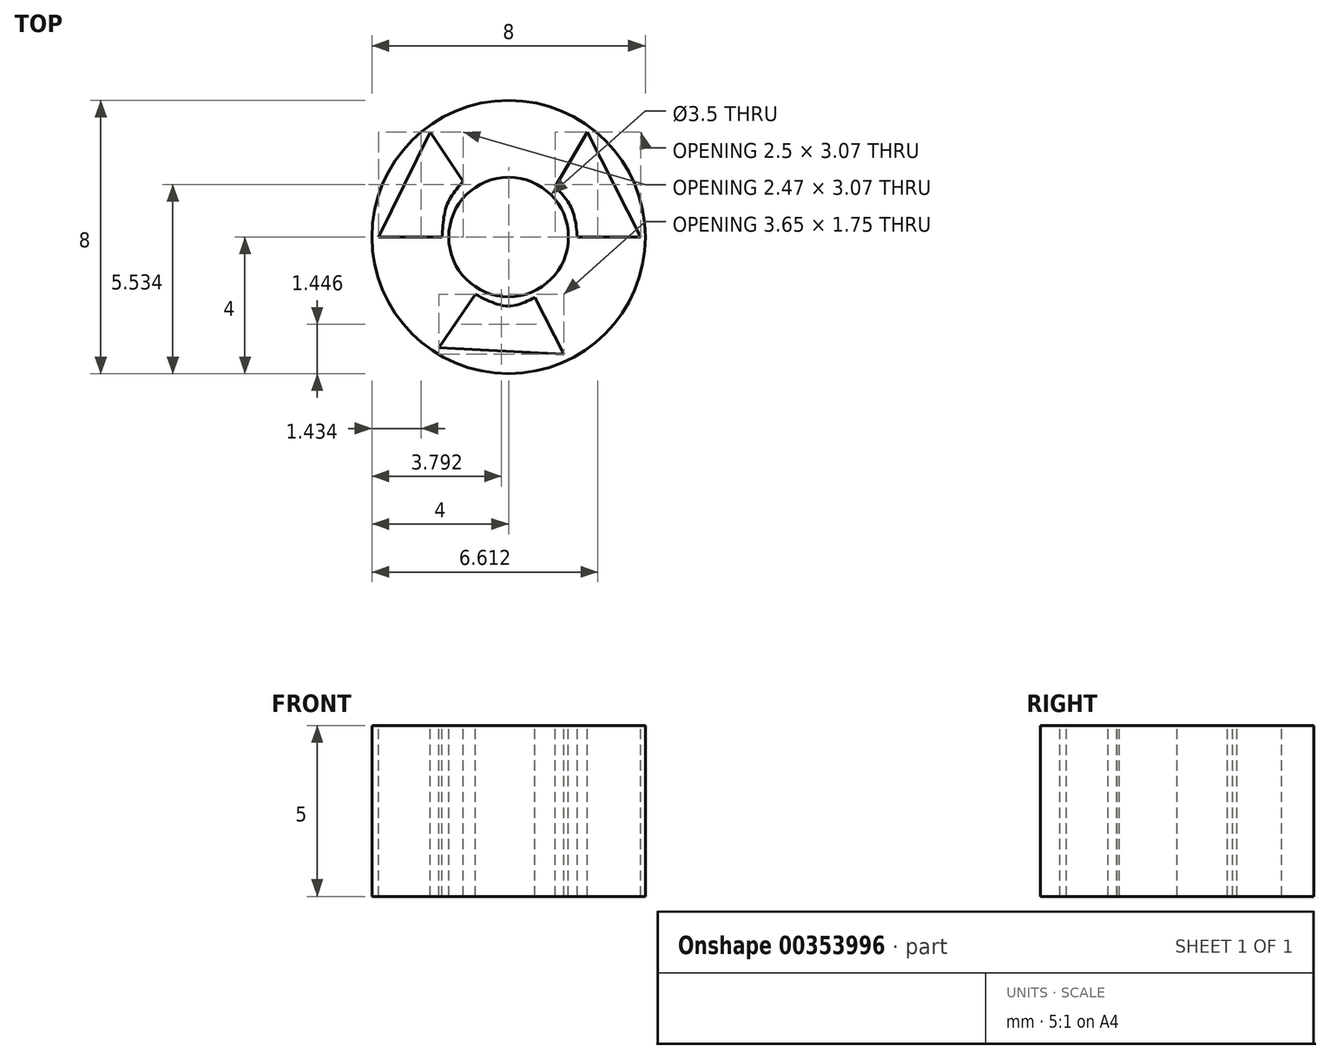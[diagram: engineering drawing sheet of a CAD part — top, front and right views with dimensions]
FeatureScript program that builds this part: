
annotation { "Feature Type Name" : "Feature", "Feature Type Description" : "" }
export const myFeature = defineFeature(function(context is Context, id is Id, definition is map)
    precondition{}
    {
        {
            var Q0;
            Q0=qCreatedBy(makeId("Top.planeOp"),FACE);
            var sketch = newSketch(context, id + "F0", { "sketchPlane" : qUnion([Q0])});
            skCircle(sketch, "E0", {"center": v(0, 0) * mm, "radius": 4 * mm});
            skSolve(sketch);
        }
        {
            var Q0;
            Q0 = qSketchRegion(id + "F0", true);
            extrude(context, id + "F1", {"entities" : qUnion([Q0]), "endBound" : BoundingType.SYMMETRIC, "depth" : 5 * mm});
        }
        {
            var Q0;
            Q0=makeQuery(id+"F1.opExtrude","CAP_FACE",FACE,{"disambiguationData":[OSD([sQuery(id+"F0.wireOp",EDGE,"E0")])],"isStart":false});
            var sketch = newSketch(context, id + "F2", { "sketchPlane" : qUnion([Q0])});
            skCircle(sketch, "E1", {"center": v(0, 0) * mm, "radius": 1.75 * mm});
            skSolve(sketch);
        }
        {
            var Q0;
            Q0=makeQuery(id+"F2.imprint","IMPRINT",FACE,{"disambiguationData":[TD([[makeQuery(id+"F2.imprint","IMPRINT",EDGE,{"derivedFrom":sQuery(id+"F2.wireOp",EDGE,"E1")}),1.0]])]});
            extrude(context, id + "F3", {"entities" : qUnion([Q0]), "operationType" : NewBodyOperationType.REMOVE, "oppositeDirection" : true, "depth" : 11.3 * mm});
        }
        {
            var Q0;
            Q0=makeQuery(id+"F1.opExtrude","CAP_FACE",FACE,{"disambiguationData":[OSD([sQuery(id+"F0.wireOp",EDGE,"E0")])],"isStart":false});
            var sketch = newSketch(context, id + "F4", { "sketchPlane" : qUnion([Q0])});
            skSolve(sketch);
        }
        {
            var Q0;
            Q0=makeQuery(id+"F4.imprint","IMPRINT",FACE,{"disambiguationData":[TD([[makeQuery(id+"F4.imprint","IMPRINT",EDGE,{"derivedFrom":makeQuery(id+"F1.opExtrude","CAP_EDGE",EDGE,{"disambiguationData":[OSD([sQuery(id+"F0.wireOp",EDGE,"E0")])],"isStart":false})}),1.0]])]});
            var sketch = newSketch(context, id + "F5", { "sketchPlane" : qUnion([Q0])});
            skLineSegment(sketch, "E2", {"start": v(2.01, 0) * mm, "end": v(3.86, 0) * mm});
            skLineSegment(sketch, "E3", {"start": v(-2.1, 0) * mm, "end": v(-3.8, 0) * mm});
            skLineSegment(sketch, "E4", {"start": v(-3.8, 0) * mm, "end": v(-2.3, 3.07) * mm});
            skLineSegment(sketch, "E5", {"start": v(3.86, 0) * mm, "end": v(2.3, 3.07) * mm});
            skLineSegment(sketch, "E6", {"start": v(-2.3, 3.07) * mm, "end": v(-1.33, 1.63) * mm});
            skLineSegment(sketch, "E7", {"start": v(2.3, 3.07) * mm, "end": v(1.36, 1.47) * mm});
            skFitSpline(sketch, "E8", {"points": [v(2.01, 0) * mm, v(1.84, 0.84) * mm, v(1.36, 1.47) * mm], "startDerivative": vector(-0.17, 1.74) * mm, "endDerivative": vector(-1.14, 1.2) * mm});
            skFitSpline(sketch, "E9", {"points": [v(-1.33, 1.63) * mm, v(-1.8, 0.96) * mm, v(-1.95, 0) * mm], "startDerivative": vector(-1.13, -1.3) * mm, "endDerivative": vector(-0.12, -1.95) * mm});
            skLineSegment(sketch, "E10", {"start": v(-2.1, 0) * mm, "end": v(-1.95, 0) * mm});
            skLineSegment(sketch, "E11", {"start": v(-2.03, -3.24) * mm, "end": v(1.62, -3.43) * mm});
            skLineSegment(sketch, "E12", {"start": v(1.62, -3.43) * mm, "end": v(0.76, -1.77) * mm});
            skLineSegment(sketch, "E13", {"start": v(-2.03, -3.24) * mm, "end": v(-0.97, -1.68) * mm});
            skFitSpline(sketch, "E14", {"points": [v(-0.97, -1.68) * mm, v(0, -2.02) * mm, v(0.76, -1.77) * mm], "startDerivative": vector(1.88, -0.95) * mm, "endDerivative": vector(1.57, 0.82) * mm});
            skSolve(sketch);
        }
        {
            var Q0;
            Q0 = qSketchRegion(id + "F5", true);
            extrude(context, id + "F6", {"entities" : qUnion([Q0]), "operationType" : NewBodyOperationType.REMOVE, "oppositeDirection" : true, "depth" : 8.5 * mm});
        }
    });
